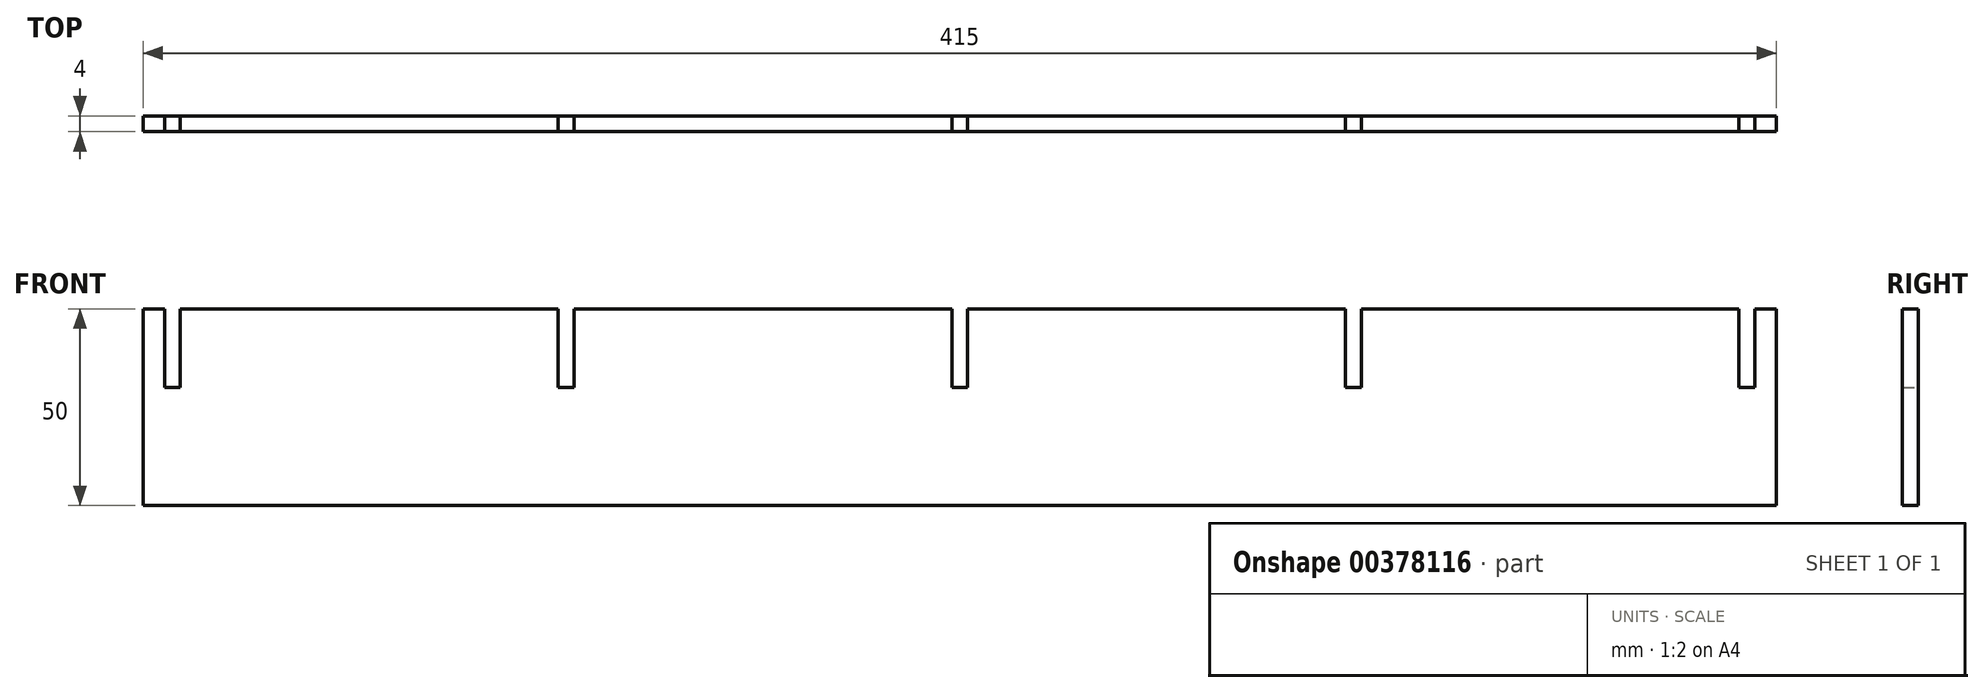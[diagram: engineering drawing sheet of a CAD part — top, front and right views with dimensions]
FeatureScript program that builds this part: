
annotation { "Feature Type Name" : "Feature", "Feature Type Description" : "" }
export const myFeature = defineFeature(function(context is Context, id is Id, definition is map)
    precondition{}
    {
        {
            var Q0;
            Q0=qCreatedBy(makeId("Front.planeOp"),FACE);
            var sketch = newSketch(context, id + "F0", { "sketchPlane" : qUnion([Q0])});
            skLineSegment(sketch, "E0", {"start": v(0, 0) * mm, "end": v(0, 50) * mm});
            skLineSegment(sketch, "E1", {"start": v(0, 50) * mm, "end": v(5.5, 50) * mm});
            skLineSegment(sketch, "E2", {"start": v(5.5, 50) * mm, "end": v(5.5, 30) * mm});
            skLineSegment(sketch, "E3", {"start": v(5.5, 30) * mm, "end": v(9.5, 30) * mm});
            skLineSegment(sketch, "E4", {"start": v(9.5, 30) * mm, "end": v(9.5, 50) * mm});
            skLineSegment(sketch, "E5", {"start": v(9.5, 50) * mm, "end": v(105.5, 50) * mm});
            skLineSegment(sketch, "E6", {"start": v(105.5, 50) * mm, "end": v(105.5, 30) * mm});
            skLineSegment(sketch, "E7", {"start": v(105.5, 30) * mm, "end": v(109.5, 30) * mm});
            skLineSegment(sketch, "E8", {"start": v(109.5, 30) * mm, "end": v(109.5, 50) * mm});
            skLineSegment(sketch, "E9", {"start": v(109.5, 50) * mm, "end": v(205.5, 50) * mm});
            skLineSegment(sketch, "E10", {"start": v(205.5, 50) * mm, "end": v(205.5, 30) * mm});
            skLineSegment(sketch, "E11", {"start": v(205.5, 30) * mm, "end": v(209.5, 30) * mm});
            skLineSegment(sketch, "E12", {"start": v(209.5, 30) * mm, "end": v(209.5, 50) * mm});
            skLineSegment(sketch, "E13", {"start": v(209.5, 50) * mm, "end": v(305.5, 50) * mm});
            skLineSegment(sketch, "E14", {"start": v(305.5, 50) * mm, "end": v(305.5, 30) * mm});
            skLineSegment(sketch, "E15", {"start": v(305.5, 30) * mm, "end": v(309.5, 30) * mm});
            skLineSegment(sketch, "E16", {"start": v(309.5, 30) * mm, "end": v(309.5, 50) * mm});
            skLineSegment(sketch, "E17", {"start": v(309.5, 50) * mm, "end": v(405.5, 50) * mm});
            skLineSegment(sketch, "E18", {"start": v(405.5, 50) * mm, "end": v(405.5, 30) * mm});
            skLineSegment(sketch, "E19", {"start": v(405.5, 30) * mm, "end": v(409.5, 30) * mm});
            skLineSegment(sketch, "E20", {"start": v(409.5, 30) * mm, "end": v(409.5, 50) * mm});
            skLineSegment(sketch, "E21", {"start": v(409.5, 50) * mm, "end": v(415, 50) * mm});
            skLineSegment(sketch, "E22", {"start": v(415, 50) * mm, "end": v(415, 0) * mm});
            skLineSegment(sketch, "E23", {"start": v(415, 0) * mm, "end": v(0, 0) * mm});
            skSolve(sketch);
        }
        {
            var Q0;
            Q0=makeQuery(id+"F0.imprint","IMPRINT",FACE,{"disambiguationData":[TD([[makeQuery(id+"F0.imprint","IMPRINT",EDGE,{"derivedFrom":sQuery(id+"F0.wireOp",EDGE,"E0")}),-1.0]])]});
            extrude(context, id + "F1", {"entities" : qUnion([Q0]), "depth" : 4 * mm});
        }
    });
